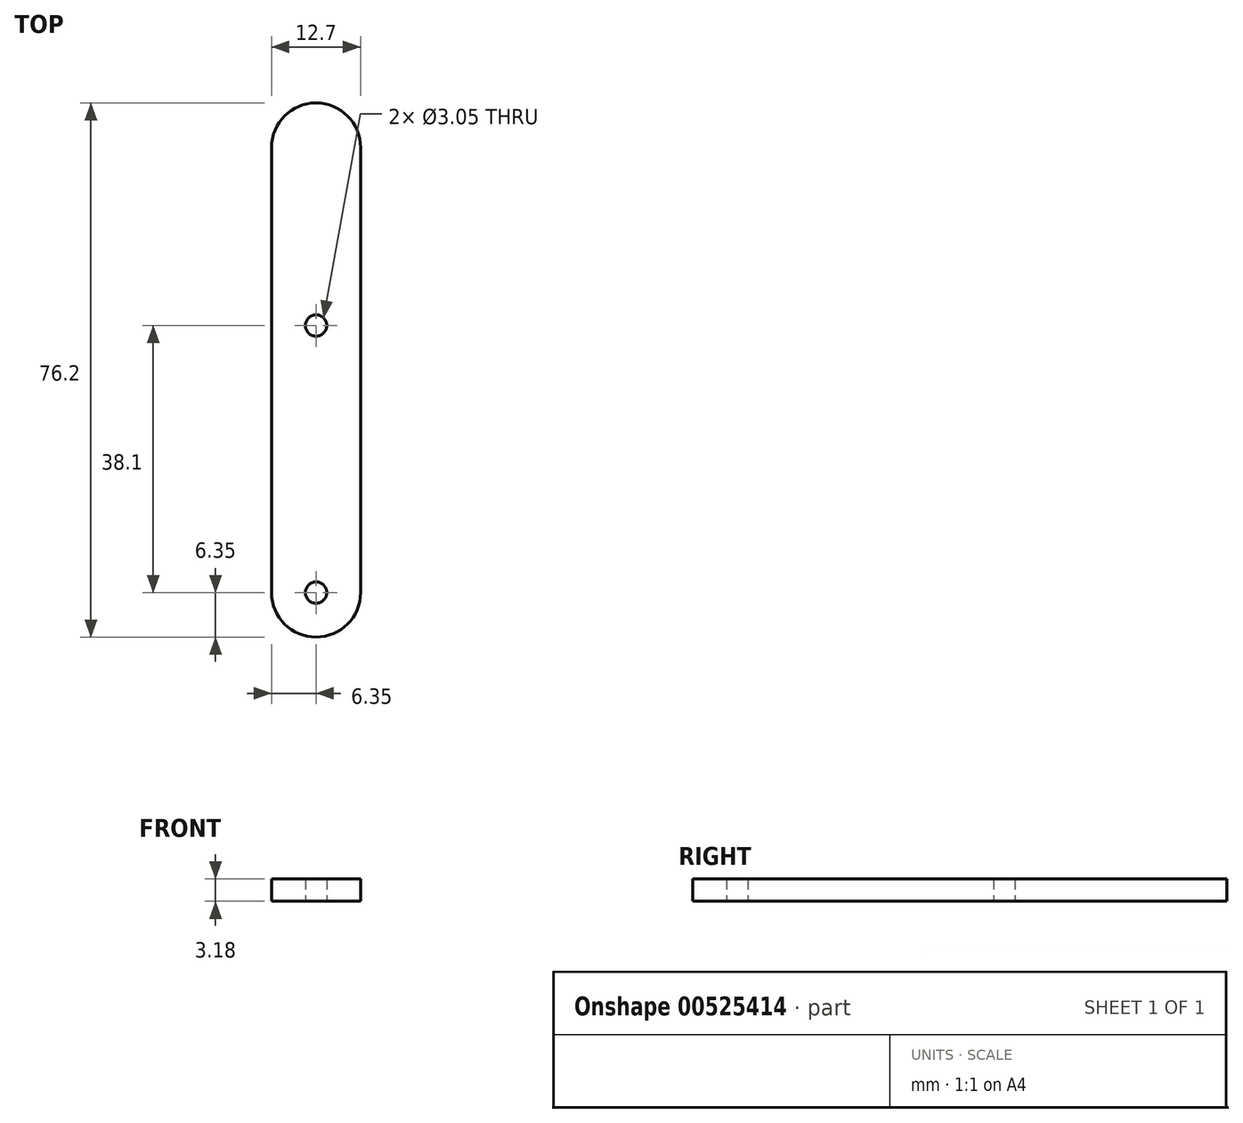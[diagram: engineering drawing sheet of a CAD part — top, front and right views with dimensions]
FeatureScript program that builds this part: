
annotation { "Feature Type Name" : "Feature", "Feature Type Description" : "" }
export const myFeature = defineFeature(function(context is Context, id is Id, definition is map)
    precondition{}
    {
        {
            var Q0;
            Q0=qCreatedBy(makeId("Top.planeOp"),FACE);
            var sketch = newSketch(context, id + "F0", { "sketchPlane" : qUnion([Q0])});
            skLineSegment(sketch, "E0.bottom", {"start": v(0, 25.4) * mm, "end": v(0, 25.4) * mm});
            skLineSegment(sketch, "E0.top", {"start": v(0, -25.4) * mm, "end": v(0, -25.4) * mm});
            skLineSegment(sketch, "E0.left", {"start": v(6.35, 25.4) * mm, "end": v(6.35, -19.05) * mm});
            skLineSegment(sketch, "E0.right", {"start": v(-6.35, 25.4) * mm, "end": v(-6.35, -19.05) * mm});
            skPoint(sketch, "E0.middle", {"position": v(0, 0) * mm});
            skCircle(sketch, "E1", {"center": v(0, -19.05) * mm, "radius": 1.52 * mm});
            skPoint(sketch, "E1.centerSnap0", {"position": v(0, -25.4) * mm});
            skCircle(sketch, "E2.MirrorC", {"center": v(0, 19.05) * mm, "radius": 1.52 * mm});
            skPoint(sketch, "E3.visualSharp", {"position": v(-6.35, 25.4) * mm});
            skPoint(sketch, "E4.visualSharp", {"position": v(6.35, 25.4) * mm});
            skPoint(sketch, "E5.visualSharp", {"position": v(6.35, -25.4) * mm});
            skArc(sketch, "E5.filletArc", {"start": v(0, -25.4) * mm, "mid": v(4.5, -23.54) * mm, "end": v(6.35, -19.05) * mm});
            skPoint(sketch, "E6.visualSharp", {"position": v(-6.35, -25.4) * mm});
            skArc(sketch, "E6.filletArc", {"start": v(-6.35, -19.05) * mm, "mid": v(-4.5, -23.54) * mm, "end": v(0, -25.4) * mm});
            skLineSegment(sketch, "E7.bottom", {"start": v(-6.35, 25.4) * mm, "end": v(6.35, 25.4) * mm});
            skLineSegment(sketch, "E7.top", {"start": v(0, 50.8) * mm, "end": v(0, 50.8) * mm});
            skLineSegment(sketch, "E7.left", {"start": v(-6.35, 25.4) * mm, "end": v(-6.35, 44.45) * mm});
            skLineSegment(sketch, "E7.right", {"start": v(6.35, 25.4) * mm, "end": v(6.35, 44.45) * mm});
            skPoint(sketch, "E8.visualSharp", {"position": v(-6.35, 50.8) * mm});
            skArc(sketch, "E8.filletArc", {"start": v(0, 50.8) * mm, "mid": v(-4.5, 48.94) * mm, "end": v(-6.35, 44.45) * mm});
            skPoint(sketch, "E9.visualSharp", {"position": v(6.35, 50.8) * mm});
            skArc(sketch, "E9.filletArc", {"start": v(6.35, 44.45) * mm, "mid": v(4.5, 48.94) * mm, "end": v(0, 50.8) * mm});
            skSolve(sketch);
        }
        {
            var Q0;
            Q0=makeQuery(id+"F0.imprint","IMPRINT",FACE,{"disambiguationData":[TD([[makeQuery(id+"F0.imprint","IMPRINT",EDGE,{"derivedFrom":sQuery(id+"F0.wireOp",EDGE,"E7.bottom")}),1.0]])]});
            var Q1;
            Q1=makeQuery(id+"F0.imprint","IMPRINT",FACE,{"disambiguationData":[TD([[makeQuery(id+"F0.imprint","IMPRINT",EDGE,{"derivedFrom":sQuery(id+"F0.wireOp",EDGE,"E0.left")}),-1.0]])]});
            extrude(context, id + "F1", {"entities" : qUnion([Q0, Q1]), "depth" : 3.17 * mm, "offsetDistance" : 25.4 * mm});
        }
    });
